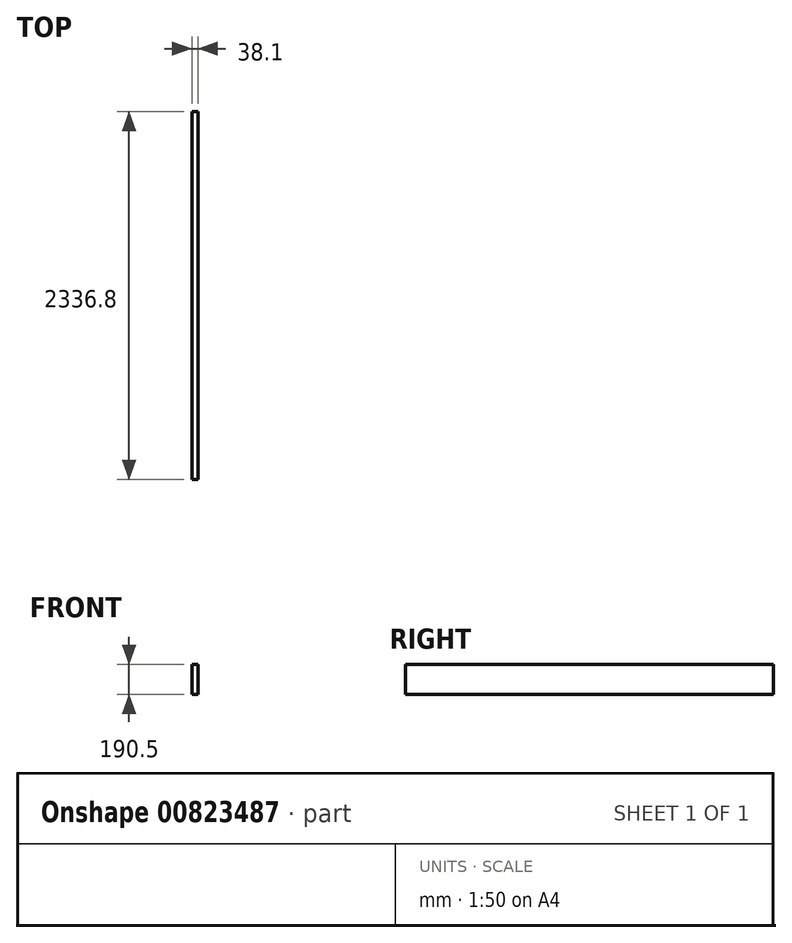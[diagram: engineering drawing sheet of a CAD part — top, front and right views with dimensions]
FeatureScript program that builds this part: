
annotation { "Feature Type Name" : "Feature", "Feature Type Description" : "" }
export const myFeature = defineFeature(function(context is Context, id is Id, definition is map)
    precondition{}
    {
        {
            var Q0;
            Q0=qCreatedBy(makeId("Front.planeOp"),FACE);
            var sketch = newSketch(context, id + "F0", { "sketchPlane" : qUnion([Q0])});
            skLineSegment(sketch, "E0.bottom", {"start": v(0, 0) * mm, "end": v(38.1, 0) * mm});
            skLineSegment(sketch, "E0.top", {"start": v(0, 190.5) * mm, "end": v(38.1, 190.5) * mm});
            skLineSegment(sketch, "E0.left", {"start": v(0, 0) * mm, "end": v(0, 190.5) * mm});
            skLineSegment(sketch, "E0.right", {"start": v(38.1, 0) * mm, "end": v(38.1, 190.5) * mm});
            skSolve(sketch);
        }
        {
            var Q0;
            Q0=qSketchRegion(id+"F0",true);
            extrude(context, id + "F1", {"entities" : qUnion([Q0]), "depth" : 2336.8 * mm, "offsetDistance" : 25.4 * mm});
        }
    });
